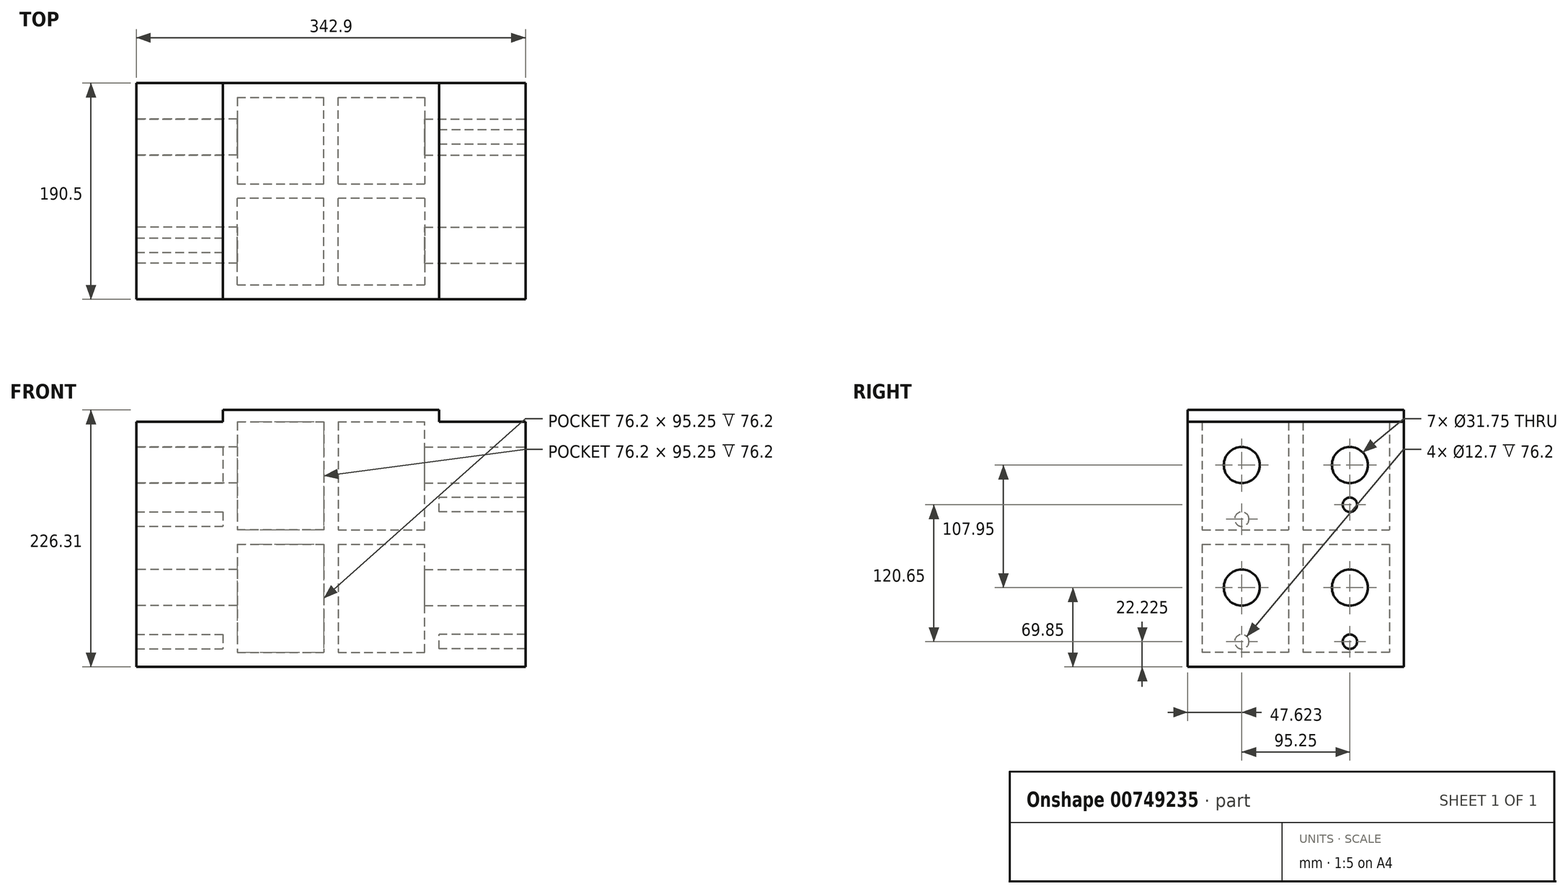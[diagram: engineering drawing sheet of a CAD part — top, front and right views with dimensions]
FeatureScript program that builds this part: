
annotation { "Feature Type Name" : "Feature", "Feature Type Description" : "" }
export const myFeature = defineFeature(function(context is Context, id is Id, definition is map)
    precondition{}
    {
        {
            var Q0;
            Q0=qCreatedBy(makeId("Top.planeOp"),FACE);
            var sketch = newSketch(context, id + "F0", { "sketchPlane" : qUnion([Q0])});
            skLineSegment(sketch, "E0.bottom", {"start": v(-75.67, 145.49) * mm, "end": v(102.13, 145.49) * mm});
            skLineSegment(sketch, "E0.top", {"start": v(-75.67, -32.31) * mm, "end": v(102.13, -32.31) * mm});
            skLineSegment(sketch, "E0.left", {"start": v(-75.67, 145.49) * mm, "end": v(-75.67, -32.31) * mm});
            skLineSegment(sketch, "E0.right", {"start": v(102.13, 145.49) * mm, "end": v(102.13, -32.31) * mm});
            skSolve(sketch);
        }
        {
            var Q0;
            Q0=makeQuery(id+"F0.imprint","IMPRINT",FACE,{"disambiguationData":[TD([[makeQuery(id+"F0.imprint","IMPRINT",EDGE,{"derivedFrom":sQuery(id+"F0.wireOp",EDGE,"E0.bottom")}),-1.0]])]});
            extrude(context, id + "F1", {"entities" : qUnion([Q0]), "depth" : 12.7 * mm, "offsetDistance" : 25.4 * mm});
        }
        {
            var Q0;
            Q0=makeQuery(id+"F1.opExtrude","SWEPT_FACE",FACE,{"disambiguationData":[OSD([sQuery(id+"F0.wireOp",EDGE,"E0.right")])]});
            var sketch = newSketch(context, id + "F2", { "sketchPlane" : qUnion([Q0])});
            skLineSegment(sketch, "E1.bottom", {"start": v(-32.31, 12.7) * mm, "end": v(145.49, 12.7) * mm});
            skLineSegment(sketch, "E1.top", {"start": v(-32.31, 215.9) * mm, "end": v(145.49, 215.9) * mm});
            skLineSegment(sketch, "E1.left", {"start": v(-32.31, 12.7) * mm, "end": v(-32.31, 215.9) * mm});
            skLineSegment(sketch, "E1.right", {"start": v(145.49, 12.7) * mm, "end": v(145.49, 215.9) * mm});
            skSolve(sketch);
        }
        {
            var Q0;
            Q0=makeQuery(id+"F2.imprint","IMPRINT",FACE,{"disambiguationData":[TD([[makeQuery(id+"F2.imprint","IMPRINT",EDGE,{"derivedFrom":sQuery(id+"F2.wireOp",EDGE,"E1.bottom")}),-1.0]])]});
            extrude(context, id + "F3", {"entities" : qUnion([Q0]), "operationType" : NewBodyOperationType.ADD, "oppositeDirection" : true, "depth" : 12.7 * mm, "offsetDistance" : 25.4 * mm});
        }
        {
            var Q0;
            Q0=makeQuery(id+"F3.boolean.opBoolean","MERGE",FACE,{"derivedFrom":[makeQuery(id+"F1.opExtrude","SWEPT_FACE",FACE,{"disambiguationData":[OSD([sQuery(id+"F0.wireOp",EDGE,"E0.bottom")])]}),makeQuery(id+"F3.opExtrude","SWEPT_FACE",FACE,{"disambiguationData":[OSD([sQuery(id+"F2.wireOp",EDGE,"E1.right")])]})]});
            var sketch = newSketch(context, id + "F4", { "sketchPlane" : qUnion([Q0])});
            skLineSegment(sketch, "E2.bottom", {"start": v(-89.43, 215.9) * mm, "end": v(75.67, 215.9) * mm});
            skLineSegment(sketch, "E2.top", {"start": v(-89.43, 12.7) * mm, "end": v(75.67, 12.7) * mm});
            skLineSegment(sketch, "E2.left", {"start": v(-89.43, 215.9) * mm, "end": v(-89.43, 12.7) * mm});
            skLineSegment(sketch, "E2.right", {"start": v(75.67, 215.9) * mm, "end": v(75.67, 12.7) * mm});
            skSolve(sketch);
        }
        {
            var Q0;
            Q0=makeQuery(id+"F4.imprint","IMPRINT",FACE,{"disambiguationData":[TD([[makeQuery(id+"F4.imprint","IMPRINT",EDGE,{"derivedFrom":sQuery(id+"F4.wireOp",EDGE,"E2.bottom")}),-1.0]])]});
            extrude(context, id + "F5", {"entities" : qUnion([Q0]), "operationType" : NewBodyOperationType.ADD, "oppositeDirection" : true, "depth" : 12.7 * mm, "offsetDistance" : 25.4 * mm});
        }
        {
            var Q0;
            Q0=makeQuery(id+"F3.opExtrude","CAP_FACE",FACE,{"disambiguationData":[OSD([sQuery(id+"F2.wireOp",EDGE,"E1.bottom"),sQuery(id+"F2.wireOp",EDGE,"E1.top"),sQuery(id+"F2.wireOp",EDGE,"E1.left"),sQuery(id+"F2.wireOp",EDGE,"E1.right")])],"isStart":false});
            var sketch = newSketch(context, id + "F6", { "sketchPlane" : qUnion([Q0])});
            skLineSegment(sketch, "E3.bottom", {"start": v(-132.79, 120.65) * mm, "end": v(32.31, 120.65) * mm});
            skLineSegment(sketch, "E3.top", {"start": v(-132.79, 107.95) * mm, "end": v(32.31, 107.95) * mm});
            skLineSegment(sketch, "E3.left", {"start": v(-132.79, 120.65) * mm, "end": v(-132.79, 107.95) * mm});
            skLineSegment(sketch, "E3.right", {"start": v(32.31, 120.65) * mm, "end": v(32.31, 107.95) * mm});
            skSolve(sketch);
        }
        {
            var Q0;
            Q0=makeQuery(id+"F6.imprint","IMPRINT",FACE,{"disambiguationData":[TD([[makeQuery(id+"F6.imprint","IMPRINT",EDGE,{"derivedFrom":sQuery(id+"F6.wireOp",EDGE,"E3.bottom")}),-1.0]])]});
            var Q1;
            Q1=makeQuery(id+"F5.boolean.opBoolean","MERGE",FACE,{"derivedFrom":[makeQuery(id+"F1.opExtrude","SWEPT_FACE",FACE,{"disambiguationData":[OSD([sQuery(id+"F0.wireOp",EDGE,"E0.left")])]}),makeQuery(id+"F5.opExtrude","SWEPT_FACE",FACE,{"disambiguationData":[OSD([sQuery(id+"F4.wireOp",EDGE,"E2.right")])]})]});
            extrude(context, id + "F7", {"entities" : qUnion([Q0]), "operationType" : NewBodyOperationType.ADD, "endBound" : BoundingType.UP_TO_SURFACE, "depth" : 25.4 * mm, "endBoundEntityFace" : qUnion([Q1]), "offsetDistance" : 25.4 * mm});
        }
        {
            var Q0;
            Q0=makeQuery(id+"F1.opExtrude","CAP_FACE",FACE,{"disambiguationData":[OSD([sQuery(id+"F0.wireOp",EDGE,"E0.bottom"),sQuery(id+"F0.wireOp",EDGE,"E0.top"),sQuery(id+"F0.wireOp",EDGE,"E0.left"),sQuery(id+"F0.wireOp",EDGE,"E0.right")])],"isStart":false});
            var sketch = newSketch(context, id + "F8", { "sketchPlane" : qUnion([Q0])});
            skLineSegment(sketch, "E4", {"start": v(89.43, 50.24) * mm, "end": v(-75.67, 50.24) * mm, "construction": true});
            skLineSegment(sketch, "E5", {"start": v(6.88, 132.79) * mm, "end": v(6.88, -32.31) * mm, "construction": true});
            skLineSegment(sketch, "E6.bottom", {"start": v(0.53, 132.79) * mm, "end": v(13.23, 132.79) * mm});
            skLineSegment(sketch, "E6.top", {"start": v(0.53, -32.31) * mm, "end": v(13.23, -32.31) * mm});
            skLineSegment(sketch, "E6.left", {"start": v(0.53, 132.79) * mm, "end": v(0.53, -32.31) * mm});
            skLineSegment(sketch, "E6.right", {"start": v(13.23, 132.79) * mm, "end": v(13.23, -32.31) * mm});
            skLineSegment(sketch, "E7.bottom", {"start": v(-75.67, 56.59) * mm, "end": v(89.43, 56.59) * mm});
            skLineSegment(sketch, "E7.top", {"start": v(-75.67, 43.89) * mm, "end": v(89.43, 43.89) * mm});
            skLineSegment(sketch, "E7.left", {"start": v(-75.67, 56.59) * mm, "end": v(-75.67, 43.89) * mm});
            skLineSegment(sketch, "E7.right", {"start": v(89.43, 56.59) * mm, "end": v(89.43, 43.89) * mm});
            skSolve(sketch);
        }
        {
            var Q0;
            {var subQ0=sQuery(id+"F8.wireOp",EDGE,"E6.bottom");Q0=makeQuery(id+"F8.imprint","IMPRINT",FACE,{"disambiguationData":[TD([[makeQuery(id+"F8.imprint","IMPRINT",EDGE,{"derivedFrom":subQ0}),-1.0]])]});}
            var Q1;
            {var subQ5=sQuery(id+"F8.wireOp",EDGE,"E7.left");Q1=makeQuery(id+"F8.imprint","IMPRINT",FACE,{"disambiguationData":[TD([[makeQuery(id+"F8.imprint","IMPRINT",EDGE,{"derivedFrom":subQ5}),1.0]])]});}
            var Q2;
            {var subQ0=sQuery(id+"F8.wireOp",EDGE,"E7.bottom");var subQ1=sQuery(id+"F8.wireOp",EDGE,"E6.left");var subQ2=makeQuery(id+"F8.imprint","INTERSECT",VERTEX,{"derivedFrom":[subQ1,subQ0]});Q2=makeQuery(id+"F8.imprint","IMPRINT",FACE,{"disambiguationData":[TD([[makeQuery(id+"F8.imprint","IMPRINT",EDGE,{"disambiguationData":[TD([[subQ2,-1.0]])],"derivedFrom":subQ1}),1.0]])]});}
            var Q3;
            {var subQ0=sQuery(id+"F8.wireOp",EDGE,"E6.top");Q3=makeQuery(id+"F8.imprint","IMPRINT",FACE,{"disambiguationData":[TD([[makeQuery(id+"F8.imprint","IMPRINT",EDGE,{"derivedFrom":subQ0}),1.0]])]});}
            var Q4;
            {var subQ5=sQuery(id+"F8.wireOp",EDGE,"E7.right");Q4=makeQuery(id+"F8.imprint","IMPRINT",FACE,{"disambiguationData":[TD([[makeQuery(id+"F8.imprint","IMPRINT",EDGE,{"derivedFrom":subQ5}),-1.0]])]});}
            var Q5;
            Q5=makeQuery(id+"F5.boolean.opBoolean","MERGE",FACE,{"derivedFrom":[makeQuery(id+"F3.opExtrude","SWEPT_FACE",FACE,{"disambiguationData":[OSD([sQuery(id+"F2.wireOp",EDGE,"E1.top")])]}),makeQuery(id+"F5.opExtrude","SWEPT_FACE",FACE,{"disambiguationData":[OSD([sQuery(id+"F4.wireOp",EDGE,"E2.bottom")])]})]});
            extrude(context, id + "F9", {"entities" : qUnion([Q0, Q1, Q2, Q3, Q4]), "operationType" : NewBodyOperationType.ADD, "endBound" : BoundingType.UP_TO_SURFACE, "depth" : 25.4 * mm, "endBoundEntityFace" : qUnion([Q5]), "offsetDistance" : 25.4 * mm});
        }
        {
            var Q0;
            Q0=makeQuery(id+"F9.boolean.opBoolean","MERGE",FACE,{"derivedFrom":[makeQuery(id+"F7.boolean.opBoolean","MERGE",FACE,{"derivedFrom":[makeQuery(id+"F5.boolean.opBoolean","MERGE",FACE,{"derivedFrom":[makeQuery(id+"F1.opExtrude","SWEPT_FACE",FACE,{"disambiguationData":[OSD([sQuery(id+"F0.wireOp",EDGE,"E0.left")])]}),makeQuery(id+"F5.opExtrude","SWEPT_FACE",FACE,{"disambiguationData":[OSD([sQuery(id+"F4.wireOp",EDGE,"E2.right")])]})]}),makeQuery(id+"F7.opExtrude","CAP_FACE",FACE,{"disambiguationData":[OSD([sQuery(id+"F6.wireOp",EDGE,"E3.bottom"),sQuery(id+"F6.wireOp",EDGE,"E3.top"),sQuery(id+"F6.wireOp",EDGE,"E3.left"),sQuery(id+"F6.wireOp",EDGE,"E3.right")])],"isStart":false})]}),makeQuery(id+"F9.opExtrude","SWEPT_FACE",FACE,{"disambiguationData":[OSD([sQuery(id+"F8.wireOp",EDGE,"E7.left")])]})]});
            var sketch = newSketch(context, id + "F10", { "sketchPlane" : qUnion([Q0])});
            skLineSegment(sketch, "E8.bottom", {"start": v(-145.49, 215.9) * mm, "end": v(32.31, 215.9) * mm});
            skLineSegment(sketch, "E8.top", {"start": v(-145.49, 0) * mm, "end": v(32.31, 0) * mm});
            skLineSegment(sketch, "E8.left", {"start": v(-145.49, 215.9) * mm, "end": v(-145.49, 0) * mm});
            skLineSegment(sketch, "E8.right", {"start": v(32.31, 215.9) * mm, "end": v(32.31, 0) * mm});
            skSolve(sketch);
        }
        {
            var Q0;
            {var subQ3=makeQuery(id+"F3.opExtrude","SWEPT_FACE",FACE,{"disambiguationData":[OSD([sQuery(id+"F2.wireOp",EDGE,"E1.top")])]});var subQ6=sQuery(id+"F4.wireOp",EDGE,"E2.right");var subQ12=makeQuery(id+"F7.boolean.opBoolean","SPLIT",EDGE,{"disambiguationData":[TD([subQ3])],"derivedFrom":makeQuery(id+"F5.opExtrude","CAP_EDGE",EDGE,{"disambiguationData":[OSD([subQ6])],"isStart":false})});Q0=makeQuery(id+"F10.imprint","IMPRINT",FACE,{"disambiguationData":[TD([[makeQuery(id+"F10.imprint","IMPRINT",EDGE,{"derivedFrom":subQ12}),1.0]])]});}
            var Q1;
            {var subQ2=sQuery(id+"F6.wireOp",EDGE,"E3.bottom");var subQ17=makeQuery(id+"F9.boolean.opBoolean","SPLIT",EDGE,{"disambiguationData":[TD([makeQuery(id+"F1.opExtrude","SWEPT_FACE",FACE,{"disambiguationData":[OSD([sQuery(id+"F0.wireOp",EDGE,"E0.top")])]})])],"derivedFrom":makeQuery(id+"F7.opExtrude","CAP_EDGE",EDGE,{"disambiguationData":[OSD([subQ2])],"isStart":false})});Q1=makeQuery(id+"F10.imprint","IMPRINT",FACE,{"disambiguationData":[TD([[makeQuery(id+"F10.imprint","IMPRINT",EDGE,{"derivedFrom":subQ17}),-1.0]])]});}
            var Q2;
            {var subQ7=sQuery(id+"F0.wireOp",EDGE,"E0.top");var subQ8=makeQuery(id+"F1.opExtrude","SWEPT_FACE",FACE,{"disambiguationData":[OSD([subQ7])]});var subQ13=sQuery(id+"F6.wireOp",EDGE,"E3.top");var subQ20=makeQuery(id+"F9.boolean.opBoolean","SPLIT",EDGE,{"disambiguationData":[TD([subQ8])],"derivedFrom":makeQuery(id+"F7.opExtrude","CAP_EDGE",EDGE,{"disambiguationData":[OSD([subQ13])],"isStart":false})});Q2=makeQuery(id+"F10.imprint","IMPRINT",FACE,{"disambiguationData":[TD([[makeQuery(id+"F10.imprint","IMPRINT",EDGE,{"derivedFrom":subQ20}),1.0]])]});}
            var Q3;
            {var subQ6=sQuery(id+"F6.wireOp",EDGE,"E3.top");var subQ10=sQuery(id+"F8.wireOp",EDGE,"E7.bottom");var subQ12=makeQuery(id+"F9.opExtrude","SWEPT_FACE",FACE,{"disambiguationData":[OSD([subQ10]),TDD([makeQuery(id+"F8.imprint","IMPRINT",EDGE,{"disambiguationData":[TD([[makeQuery(id+"F8.imprint","INTERSECT",VERTEX,{"derivedFrom":[sQuery(id+"F8.wireOp",EDGE,"E6.left"),subQ10]}),1.0]])],"derivedFrom":subQ10})])]});Q3=makeQuery(id+"F10.imprint","IMPRINT",FACE,{"disambiguationData":[TD([[makeQuery(id+"F10.imprint","IMPRINT",EDGE,{"derivedFrom":makeQuery(id+"F9.boolean.opBoolean","SPLIT",EDGE,{"disambiguationData":[TD([subQ12])],"derivedFrom":makeQuery(id+"F7.opExtrude","CAP_EDGE",EDGE,{"disambiguationData":[OSD([subQ6])],"isStart":false})})}),1.0]])]});}
            var Q4;
            {var subQ36=sQuery(id+"F10.wireOp",EDGE,"E8.top");Q4=makeQuery(id+"F10.imprint","IMPRINT",FACE,{"disambiguationData":[TD([[makeQuery(id+"F10.imprint","IMPRINT",EDGE,{"derivedFrom":subQ36}),1.0]])]});}
            extrude(context, id + "F11", {"entities" : qUnion([Q0, Q1, Q2, Q3, Q4]), "operationType" : NewBodyOperationType.ADD, "depth" : 12.7 * mm, "offsetDistance" : 25.4 * mm});
        }
        {
            var Q0;
            Q0=makeQuery(id+"F11.boolean.opBoolean","MERGE",FACE,{"derivedFrom":[makeQuery(id+"F9.boolean.opBoolean","MERGE",FACE,{"derivedFrom":[makeQuery(id+"F7.boolean.opBoolean","MERGE",FACE,{"derivedFrom":[makeQuery(id+"F3.boolean.opBoolean","MERGE",FACE,{"derivedFrom":[makeQuery(id+"F1.opExtrude","SWEPT_FACE",FACE,{"disambiguationData":[OSD([sQuery(id+"F0.wireOp",EDGE,"E0.top")])]}),makeQuery(id+"F3.opExtrude","SWEPT_FACE",FACE,{"disambiguationData":[OSD([sQuery(id+"F2.wireOp",EDGE,"E1.left")])]})]}),makeQuery(id+"F7.opExtrude","SWEPT_FACE",FACE,{"disambiguationData":[OSD([sQuery(id+"F6.wireOp",EDGE,"E3.right")])]})]}),makeQuery(id+"F9.opExtrude","SWEPT_FACE",FACE,{"disambiguationData":[OSD([sQuery(id+"F8.wireOp",EDGE,"E6.top")])]})]}),makeQuery(id+"F11.opExtrude","SWEPT_FACE",FACE,{"disambiguationData":[OSD([sQuery(id+"F10.wireOp",EDGE,"E8.right")])]})]});
            var sketch = newSketch(context, id + "F12", { "sketchPlane" : qUnion([Q0])});
            skLineSegment(sketch, "E9.bottom", {"start": v(-88.37, 215.9) * mm, "end": v(102.13, 215.9) * mm});
            skLineSegment(sketch, "E9.top", {"start": v(-88.37, 0) * mm, "end": v(102.13, 0) * mm});
            skLineSegment(sketch, "E9.left", {"start": v(-88.37, 215.9) * mm, "end": v(-88.37, 0) * mm});
            skLineSegment(sketch, "E9.right", {"start": v(102.13, 215.9) * mm, "end": v(102.13, 0) * mm});
            skSolve(sketch);
        }
        {
            var Q0;
            {var subQ2=sQuery(id+"F2.wireOp",EDGE,"E1.left");var subQ4=sQuery(id+"F6.wireOp",EDGE,"E3.right");var subQ9=sQuery(id+"F6.wireOp",EDGE,"E3.bottom");Q0=makeQuery(id+"F12.imprint","IMPRINT",FACE,{"disambiguationData":[TD([[makeQuery(id+"F12.imprint","IMPRINT",EDGE,{"derivedFrom":makeQuery(id+"F9.boolean.opBoolean","SPLIT",EDGE,{"disambiguationData":[TD([makeQuery(id+"F1.opExtrude","SWEPT_FACE",FACE,{"disambiguationData":[OSD([sQuery(id+"F0.wireOp",EDGE,"E0.left")])]})])],"derivedFrom":makeQuery(id+"F7.opExtrude","SWEPT_EDGE",EDGE,{"disambiguationData":[OSD([subQ2,subQ9,subQ4])]})})}),1.0]])]});}
            var Q1;
            {var subQ1=sQuery(id+"F2.wireOp",EDGE,"E1.left");var subQ5=sQuery(id+"F2.wireOp",EDGE,"E1.top");var subQ6=makeQuery(id+"F3.opExtrude","SWEPT_FACE",FACE,{"disambiguationData":[OSD([subQ5])]});var subQ13=makeQuery(id+"F7.boolean.opBoolean","SPLIT",EDGE,{"disambiguationData":[TD([subQ6])],"derivedFrom":makeQuery(id+"F3.opExtrude","CAP_EDGE",EDGE,{"disambiguationData":[OSD([subQ1])],"isStart":false})});Q1=makeQuery(id+"F12.imprint","IMPRINT",FACE,{"disambiguationData":[TD([[makeQuery(id+"F12.imprint","IMPRINT",EDGE,{"derivedFrom":subQ13}),1.0]])]});}
            var Q2;
            {var subQ0=sQuery(id+"F2.wireOp",EDGE,"E1.left");var subQ4=sQuery(id+"F6.wireOp",EDGE,"E3.top");var subQ5=makeQuery(id+"F7.opExtrude","SWEPT_FACE",FACE,{"disambiguationData":[OSD([subQ4])]});Q2=makeQuery(id+"F12.imprint","IMPRINT",FACE,{"disambiguationData":[TD([[makeQuery(id+"F12.imprint","IMPRINT",EDGE,{"derivedFrom":makeQuery(id+"F7.boolean.opBoolean","SPLIT",EDGE,{"disambiguationData":[TD([subQ5])],"derivedFrom":makeQuery(id+"F3.opExtrude","CAP_EDGE",EDGE,{"disambiguationData":[OSD([subQ0])],"isStart":false})})}),1.0]])]});}
            var Q3;
            {var subQ2=sQuery(id+"F0.wireOp",EDGE,"E0.top");var subQ9=sQuery(id+"F6.wireOp",EDGE,"E3.top");var subQ12=sQuery(id+"F8.wireOp",EDGE,"E6.top");var subQ14=sQuery(id+"F8.wireOp",EDGE,"E6.left");var subQ18=makeQuery(id+"F7.opExtrude","SWEPT_FACE",FACE,{"disambiguationData":[OSD([subQ9])]});Q3=makeQuery(id+"F12.imprint","IMPRINT",FACE,{"disambiguationData":[TD([[makeQuery(id+"F12.imprint","IMPRINT",EDGE,{"derivedFrom":makeQuery(id+"F9.boolean.opBoolean","SPLIT",EDGE,{"disambiguationData":[TD([subQ18])],"derivedFrom":makeQuery(id+"F9.opExtrude","SWEPT_EDGE",EDGE,{"disambiguationData":[OSD([subQ2,subQ12,subQ14])]})})}),-1.0]])]});}
            var Q4;
            Q4=makeQuery(id+"F12.imprint","IMPRINT",FACE,{"disambiguationData":[TD([[makeQuery(id+"F12.imprint","IMPRINT",EDGE,{"derivedFrom":sQuery(id+"F12.wireOp",EDGE,"E9.top")}),1.0]])]});
            extrude(context, id + "F13", {"entities" : qUnion([Q0, Q1, Q2, Q3, Q4]), "operationType" : NewBodyOperationType.ADD, "depth" : 12.7 * mm, "offsetDistance" : 25.4 * mm});
        }
        {
            var Q0;
            Q0=makeQuery(id+"F13.boolean.opBoolean","MERGE",FACE,{"derivedFrom":[makeQuery(id+"F3.boolean.opBoolean","MERGE",FACE,{"derivedFrom":[makeQuery(id+"F1.opExtrude","SWEPT_FACE",FACE,{"disambiguationData":[OSD([sQuery(id+"F0.wireOp",EDGE,"E0.right")])]}),makeQuery(id+"F3.opExtrude","CAP_FACE",FACE,{"disambiguationData":[OSD([sQuery(id+"F2.wireOp",EDGE,"E1.bottom"),sQuery(id+"F2.wireOp",EDGE,"E1.top"),sQuery(id+"F2.wireOp",EDGE,"E1.left"),sQuery(id+"F2.wireOp",EDGE,"E1.right")])],"isStart":true})]}),makeQuery(id+"F13.opExtrude","SWEPT_FACE",FACE,{"disambiguationData":[OSD([sQuery(id+"F12.wireOp",EDGE,"E9.right")])]})]});
            var sketch = newSketch(context, id + "F14", { "sketchPlane" : qUnion([Q0])});
            skLineSegment(sketch, "E10", {"start": v(50.24, 215.9) * mm, "end": v(50.24, 0) * mm, "construction": true});
            skLineSegment(sketch, "E11", {"start": v(-45.01, 107.95) * mm, "end": v(145.49, 107.95) * mm, "construction": true});
            skLineSegment(sketch, "E12", {"start": v(2.61, 215.9) * mm, "end": v(2.61, 0) * mm, "construction": true});
            skLineSegment(sketch, "E13.MirrorCS", {"start": v(97.86, 215.9) * mm, "end": v(97.86, 0) * mm, "construction": true});
            skLineSegment(sketch, "E14", {"start": v(-45.01, 161.92) * mm, "end": v(145.49, 161.92) * mm, "construction": true});
            skCircle(sketch, "E15", {"center": v(2.61, 177.8) * mm, "radius": 15.88 * mm});
            skCircle(sketch, "E16.MirrorC", {"center": v(97.86, 177.8) * mm, "radius": 15.88 * mm});
            skLineSegment(sketch, "E17.MirrorCS", {"start": v(-45.01, 53.97) * mm, "end": v(145.49, 53.97) * mm, "construction": true});
            skCircle(sketch, "E18", {"center": v(2.61, 69.85) * mm, "radius": 15.88 * mm});
            skCircle(sketch, "E19", {"center": v(97.86, 69.85) * mm, "radius": 15.88 * mm});
            skCircle(sketch, "E20", {"center": v(2.61, 142.87) * mm, "radius": 6.35 * mm});
            skCircle(sketch, "E21", {"center": v(2.61, 22.22) * mm, "radius": 6.35 * mm});
            skCircle(sketch, "E22.MirrorC", {"center": v(97.86, 142.87) * mm, "radius": 6.35 * mm});
            skCircle(sketch, "E23.MirrorC", {"center": v(97.86, 22.22) * mm, "radius": 6.35 * mm});
            skSolve(sketch);
        }
        {
            var Q0;
            Q0=sQuery(id+"F14.wireOp",VERTEX,"E15.center");
            var Q1;
            Q1=sQuery(id+"F14.wireOp",VERTEX,"E16.MirrorC.center");
            var Q2;
            Q2=sQuery(id+"F14.wireOp",VERTEX,"E18.center");
            var Q3;
            Q3=sQuery(id+"F14.wireOp",VERTEX,"E19.center");
            var Q4;
            Q4=makeQuery(id+"F1.opExtrude","SWEPT_BODY",BODY,{"disambiguationData":[OSD([sQuery(id+"F0.wireOp",EDGE,"E0.bottom"),sQuery(id+"F0.wireOp",EDGE,"E0.top"),sQuery(id+"F0.wireOp",EDGE,"E0.left"),sQuery(id+"F0.wireOp",EDGE,"E0.right")])]});
            hole(context, id + "F15", {"style" : HoleStyle.SIMPLE, "endStyle" : HoleEndStyle.BLIND, "holeDiameter" : 31.75 * mm, "majorDiameter" : 6.35 * mm, "holeDepth" : 12.7 * mm, "isTappedThrough" : true, "tappedDepth" : 12.7 * mm, "tapClearance" : 3, "locations" : qUnion([Q0, Q1, Q2, Q3]), "scope" : qUnion([Q4])});
        }
        {
            var Q0;
            Q0=makeQuery(id+"F13.boolean.opBoolean","MERGE",FACE,{"derivedFrom":[makeQuery(id+"F11.opExtrude","CAP_FACE",FACE,{"disambiguationData":[OSD([sQuery(id+"F10.wireOp",EDGE,"E8.bottom"),sQuery(id+"F10.wireOp",EDGE,"E8.top"),sQuery(id+"F10.wireOp",EDGE,"E8.left"),sQuery(id+"F10.wireOp",EDGE,"E8.right")])],"isStart":false}),makeQuery(id+"F13.opExtrude","SWEPT_FACE",FACE,{"disambiguationData":[OSD([sQuery(id+"F12.wireOp",EDGE,"E9.left")])]})]});
            var sketch = newSketch(context, id + "F16", { "sketchPlane" : qUnion([Q0])});
            skLineSegment(sketch, "E24", {"start": v(-145.49, 107.95) * mm, "end": v(45.01, 107.95) * mm, "construction": true});
            skLineSegment(sketch, "E25", {"start": v(-145.49, 161.92) * mm, "end": v(45.01, 161.92) * mm, "construction": true});
            skLineSegment(sketch, "E26", {"start": v(-50.24, 215.9) * mm, "end": v(-50.24, 0) * mm, "construction": true});
            skLineSegment(sketch, "E27", {"start": v(-97.86, 215.9) * mm, "end": v(-97.86, 0) * mm, "construction": true});
            skCircle(sketch, "E28", {"center": v(-97.86, 177.8) * mm, "radius": 15.88 * mm});
            skCircle(sketch, "E29.MirrorC", {"center": v(-2.61, 177.8) * mm, "radius": 15.88 * mm});
            skLineSegment(sketch, "E30", {"start": v(-145.49, 53.97) * mm, "end": v(-50.24, 53.97) * mm, "construction": true});
            skCircle(sketch, "E31", {"center": v(-97.86, 69.85) * mm, "radius": 15.88 * mm});
            skCircle(sketch, "E32.MirrorC", {"center": v(-2.61, 69.85) * mm, "radius": 15.88 * mm});
            skLineSegment(sketch, "E33.MirrorCS", {"start": v(45.01, 53.97) * mm, "end": v(-50.24, 53.97) * mm, "construction": true});
            skLineSegment(sketch, "E34.MirrorCS", {"start": v(-2.61, 215.9) * mm, "end": v(-2.61, 0) * mm, "construction": true});
            skLineSegment(sketch, "E35", {"start": v(-50.24, 215.9) * mm, "end": v(-50.24, 254) * mm, "construction": true});
            skCircle(sketch, "E36", {"center": v(-97.86, 130.17) * mm, "radius": 6.35 * mm});
            skCircle(sketch, "E37", {"center": v(-97.86, 22.22) * mm, "radius": 6.35 * mm});
            skCircle(sketch, "E38.MirrorC", {"center": v(-2.61, 130.17) * mm, "radius": 6.35 * mm});
            skCircle(sketch, "E39.MirrorC", {"center": v(-2.61, 22.22) * mm, "radius": 6.35 * mm});
            skSolve(sketch);
        }
        {
            var Q0;
            Q0=sQuery(id+"F16.wireOp",VERTEX,"E28.center");
            var Q1;
            Q1=sQuery(id+"F16.wireOp",VERTEX,"E29.MirrorC.center");
            var Q2;
            Q2=sQuery(id+"F16.wireOp",VERTEX,"E31.center");
            var Q3;
            Q3=sQuery(id+"F16.wireOp",VERTEX,"E32.MirrorC.center");
            var Q4;
            Q4=makeQuery(id+"F1.opExtrude","SWEPT_BODY",BODY,{"disambiguationData":[OSD([sQuery(id+"F0.wireOp",EDGE,"E0.bottom"),sQuery(id+"F0.wireOp",EDGE,"E0.top"),sQuery(id+"F0.wireOp",EDGE,"E0.left"),sQuery(id+"F0.wireOp",EDGE,"E0.right")])]});
            hole(context, id + "F17", {"style" : HoleStyle.SIMPLE, "endStyle" : HoleEndStyle.BLIND, "holeDiameter" : 31.75 * mm, "majorDiameter" : 6.35 * mm, "holeDepth" : 12.7 * mm, "isTappedThrough" : true, "tappedDepth" : 12.7 * mm, "tapClearance" : 3, "locations" : qUnion([Q0, Q1, Q2, Q3]), "scope" : qUnion([Q4])});
        }
        {
            var Q0;
            Q0=makeQuery(id+"F13.boolean.opBoolean","MERGE",FACE,{"derivedFrom":[makeQuery(id+"F11.boolean.opBoolean","MERGE",FACE,{"derivedFrom":[makeQuery(id+"F9.boolean.opBoolean","MERGE",FACE,{"derivedFrom":[makeQuery(id+"F5.boolean.opBoolean","MERGE",FACE,{"derivedFrom":[makeQuery(id+"F3.opExtrude","SWEPT_FACE",FACE,{"disambiguationData":[OSD([sQuery(id+"F2.wireOp",EDGE,"E1.top")])]}),makeQuery(id+"F5.opExtrude","SWEPT_FACE",FACE,{"disambiguationData":[OSD([sQuery(id+"F4.wireOp",EDGE,"E2.bottom")])]})]}),makeQuery(id+"F9.opExtrude","CAP_FACE",FACE,{"disambiguationData":[OSD([sQuery(id+"F8.wireOp",EDGE,"E6.bottom"),sQuery(id+"F8.wireOp",EDGE,"E6.top"),sQuery(id+"F8.wireOp",EDGE,"E6.left"),sQuery(id+"F8.wireOp",EDGE,"E6.right"),sQuery(id+"F8.wireOp",EDGE,"E7.bottom"),sQuery(id+"F8.wireOp",EDGE,"E7.top"),sQuery(id+"F8.wireOp",EDGE,"E7.left"),sQuery(id+"F8.wireOp",EDGE,"E7.right")])],"isStart":false})]}),makeQuery(id+"F11.opExtrude","SWEPT_FACE",FACE,{"disambiguationData":[OSD([sQuery(id+"F10.wireOp",EDGE,"E8.bottom")])]})]}),makeQuery(id+"F13.opExtrude","SWEPT_FACE",FACE,{"disambiguationData":[OSD([sQuery(id+"F12.wireOp",EDGE,"E9.bottom")])]})]});
            var sketch = newSketch(context, id + "F18", { "sketchPlane" : qUnion([Q0])});
            skLineSegment(sketch, "E40.bottom", {"start": v(102.13, 145.49) * mm, "end": v(-88.37, 145.49) * mm});
            skLineSegment(sketch, "E40.top", {"start": v(102.13, -45.01) * mm, "end": v(-88.37, -45.01) * mm});
            skLineSegment(sketch, "E40.left", {"start": v(102.13, 145.49) * mm, "end": v(102.13, -45.01) * mm});
            skLineSegment(sketch, "E40.right", {"start": v(-88.37, 145.49) * mm, "end": v(-88.37, -45.01) * mm});
            skPoint(sketch, "E40.middle", {"position": v(6.88, 50.24) * mm});
            skPoint(sketch, "E40.middle.positionSnap0", {"position": v(102.13, 50.24) * mm});
            skPoint(sketch, "E40.middle.positionSnap1", {"position": v(6.88, 145.49) * mm});
            skPoint(sketch, "E40.centerSnap0", {"position": v(102.13, 50.24) * mm});
            skPoint(sketch, "E40.centerSnap1", {"position": v(6.88, 145.49) * mm});
            skSolve(sketch);
        }
        {
            var Q0;
            Q0 = qSketchRegion(id + "F18", true);
            extrude(context, id + "F19", {"entities" : qUnion([Q0]), "operationType" : NewBodyOperationType.ADD, "depth" : 10.4 * mm, "offsetDistance" : 25.4 * mm});
        }
        {
            var Q0;
            Q0=makeQuery(id+"F14.imprint","IMPRINT",FACE,{"disambiguationData":[TD([[makeQuery(id+"F14.imprint","IMPRINT",EDGE,{"derivedFrom":sQuery(id+"F14.wireOp",EDGE,"E20")}),1.0]])]});
            var Q1;
            Q1=makeQuery(id+"F14.imprint","IMPRINT",FACE,{"disambiguationData":[TD([[makeQuery(id+"F14.imprint","IMPRINT",EDGE,{"derivedFrom":sQuery(id+"F14.wireOp",EDGE,"E21")}),1.0]])]});
            var Q2;
            Q2=makeQuery(id+"F14.imprint","IMPRINT",FACE,{"disambiguationData":[TD([[makeQuery(id+"F14.imprint","IMPRINT",EDGE,{"derivedFrom":sQuery(id+"F14.wireOp",EDGE,"E22.MirrorC")}),-1.0]])]});
            var Q3;
            Q3=makeQuery(id+"F14.imprint","IMPRINT",FACE,{"disambiguationData":[TD([[makeQuery(id+"F14.imprint","IMPRINT",EDGE,{"derivedFrom":sQuery(id+"F14.wireOp",EDGE,"E23.MirrorC")}),-1.0]])]});
            extrude(context, id + "F20", {"entities" : qUnion([Q0, Q1, Q2, Q3]), "operationType" : NewBodyOperationType.ADD, "depth" : 76.2 * mm, "offsetDistance" : 25.4 * mm});
        }
        {
            var Q0;
            Q0=makeQuery(id+"F16.imprint","IMPRINT",FACE,{"disambiguationData":[TD([[makeQuery(id+"F16.imprint","IMPRINT",EDGE,{"derivedFrom":sQuery(id+"F16.wireOp",EDGE,"E36")}),1.0]])]});
            var Q1;
            Q1=makeQuery(id+"F16.imprint","IMPRINT",FACE,{"disambiguationData":[TD([[makeQuery(id+"F16.imprint","IMPRINT",EDGE,{"derivedFrom":sQuery(id+"F16.wireOp",EDGE,"E37")}),1.0]])]});
            var Q2;
            Q2=makeQuery(id+"F16.imprint","IMPRINT",FACE,{"disambiguationData":[TD([[makeQuery(id+"F16.imprint","IMPRINT",EDGE,{"derivedFrom":sQuery(id+"F16.wireOp",EDGE,"E38.MirrorC")}),-1.0]])]});
            var Q3;
            Q3=makeQuery(id+"F16.imprint","IMPRINT",FACE,{"disambiguationData":[TD([[makeQuery(id+"F16.imprint","IMPRINT",EDGE,{"derivedFrom":sQuery(id+"F16.wireOp",EDGE,"E39.MirrorC")}),-1.0]])]});
            extrude(context, id + "F21", {"entities" : qUnion([Q0, Q1, Q2, Q3]), "operationType" : NewBodyOperationType.ADD, "depth" : 76.2 * mm, "offsetDistance" : 25.4 * mm});
        }
    });
